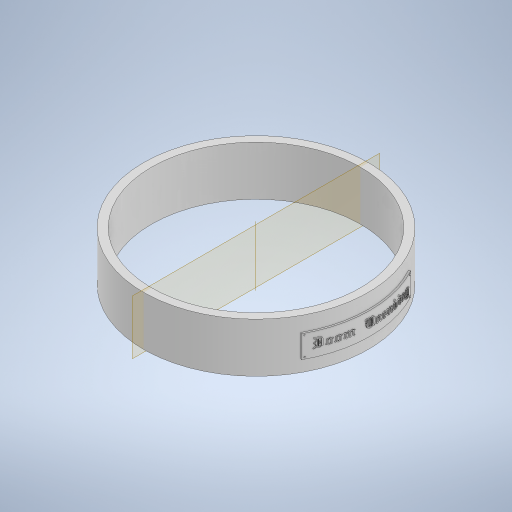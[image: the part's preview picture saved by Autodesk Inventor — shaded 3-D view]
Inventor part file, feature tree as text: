
AUTODESK INVENTOR PART (.ipt)
format: ipt  version: 2023 (Build 270158000, 158)  size: 4,118,016 bytes
history: native  units: in
note: dims shown in document units (in); Inventor stores cm internally (conversion verified against a paired STEP export)
features: emboss x3, pattern_circular x3, other x2, extrude x1, plane x1, fillet x1, sketch x1
ambient origin geometry x8: Origin, YZ Plane, XZ Plane, XY Plane, X Axis, Y Axis, Z Axis, Center Point
bodies: Solid1 (feature_tree)
feature tree (12):
  extrude  "Extrusion1"  Depth=1.9685in
  plane  "Work Plane1"
  other  "Text"
  emboss  "Emboss4"
  emboss  "Emboss5"
  emboss  "Emboss6"
  fillet  "Rivots"  Radius=0.8661in
  pattern_circular  "Circular Pattern1"  Count=6  [1 undecoded]
  pattern_circular  "Circular Pattern2"  [2 undecoded]
  pattern_circular  "Circular Pattern3"  [2 undecoded]
  sketch  "Sketch1"  dims[d0=3.937in d1=3.6614in d2=0.8661in d3=0.0in d4=2.3622in d6=0.4546in d10=0.0in d11=0.3937in d12=1.9685in d19=0.0in d20=0.0in d21=0.0295in d22=0.0in d23=0.0197in d24=0.0in d25=0.0295in d26=0.0295in d27=0.0295in d28=0.0157in d29=0.0in d30=0.0138in d31=0.7874in d32=360.0deg d34=0.7874in d35=360.0deg d37=0.7874in d38=360.0deg d33=0.0in]
  other  "NamePlate"
note: 5 required parameter values undecoded (feature->parameter linkage not recoverable at this tier; creation-order binding heuristic only, values carry confidence <= 0.55)
